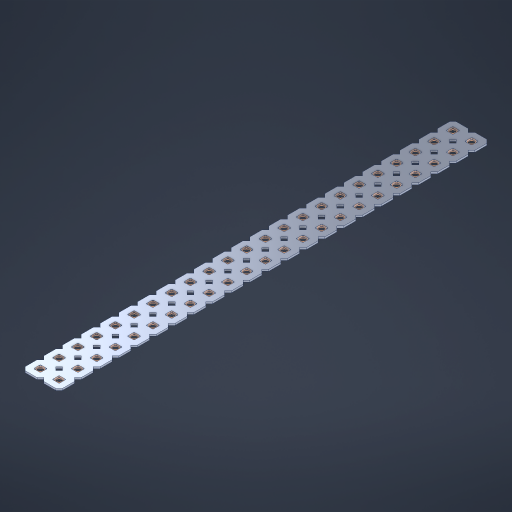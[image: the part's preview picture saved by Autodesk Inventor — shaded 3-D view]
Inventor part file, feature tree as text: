
AUTODESK INVENTOR PART (.ipt)
format: ipt  version: 2023 (Build 270158000, 158)  size: 791,040 bytes
history: native  units: in
note: dims shown in document units (in); Inventor stores cm internally (conversion verified against a paired STEP export)
features: other x47, extrude x45, sketch x2, pattern_linear x1
ambient origin geometry x8: Origin, YZ Plane, XZ Plane, XY Plane, X Axis, Y Axis, Z Axis, Center Point
bodies: Solid1 (feature_tree), Body (feature_tree)
feature tree (95):
  pattern_linear  "Rectangular Pattern1"  Spacing1=0.09in  [1 undecoded]
  sketch  "Sketch1"  dims[d1=0.5in]
  sketch  "Sketch2"  dims[d2=0.182in d3=0.09in d4=0.09in d5=0.09in d6=0.09in d7=0.09in d8=0.09in d9=0.09in d10=0.09in d11=0.02in d13=0.0in d14=0.172in d15=0.0625in d16=0.0in d19=0.5in d22=0.5in]
  other  "Srf1"
  other  "Srf126"
  other  "Srf127"
  other  "Srf128"
  other  "Srf129"
  other  "Srf130"
  other  "Srf131"
  other  "Srf250"
  other  "Srf251"
  other  "Srf252"
  other  "Srf253"
  other  "Srf254"
  other  "Srf255"
  other  "Srf256"
  other  "Srf257"
  other  "Srf258"
  other  "Srf259"
  other  "Srf260"
  other  "Srf261"
  other  "Srf262"
  other  "Srf263"
  other  "Srf264"
  other  "Srf265"
  other  "Srf268"
  other  "Srf269"
  other  "Srf270"
  other  "Srf271"
  other  "Srf272"
  other  "Srf273"
  other  "Srf274"
  other  "Srf275"
  other  "Srf276"
  other  "Srf277"
  other  "Srf278"
  other  "Srf279"
  other  "Srf280"
  other  "Srf281"
  other  "Srf282"
  other  "Srf283"
  other  "Srf284"
  other  "Srf285"
  other  "Srf286"
  other  "Srf287"
  other  "Srf288"
  other  "Srf289"
  other  "Srf290"
  other  "Circle"
  extrude  "ExtrusionSrf126"  Depth=0.09in
  extrude  "ExtrusionSrf127"  Depth=0.09in
  extrude  "ExtrusionSrf128"  Depth=0.09in
  extrude  "ExtrusionSrf129"  Depth=0.09in
  extrude  "ExtrusionSrf130"  Depth=0.09in
  extrude  "ExtrusionSrf131"  Depth=0.09in
  extrude  "ExtrusionSrf250"  Depth=0.09in
  extrude  "ExtrusionSrf251"  Depth=0.02in
  extrude  "ExtrusionSrf252"  TaperAngle=0.0deg  [1 undecoded]
  extrude  "ExtrusionSrf253"  Depth=0.5in
  extrude  "ExtrusionSrf254"  Depth=0.5in TaperAngle=0.0deg
  extrude  "ExtrusionSrf255"  Depth=0.5in
  extrude  "ExtrusionSrf256"  Depth=0.5in
  extrude  "ExtrusionSrf257"  [1 undecoded]
  extrude  "ExtrusionSrf258"  [1 undecoded]
  extrude  "ExtrusionSrf259"  [1 undecoded]
  extrude  "ExtrusionSrf260"  [1 undecoded]
  extrude  "ExtrusionSrf261"  [1 undecoded]
  extrude  "ExtrusionSrf262"  [1 undecoded]
  extrude  "ExtrusionSrf263"  [1 undecoded]
  extrude  "ExtrusionSrf264"  [1 undecoded]
  extrude  "ExtrusionSrf265"  [1 undecoded]
  extrude  "ExtrusionSrf268"  [1 undecoded]
  extrude  "ExtrusionSrf269"  [1 undecoded]
  extrude  "ExtrusionSrf270"  [1 undecoded]
  extrude  "ExtrusionSrf271"  [1 undecoded]
  extrude  "ExtrusionSrf272"  [1 undecoded]
  extrude  "ExtrusionSrf273"  [1 undecoded]
  extrude  "ExtrusionSrf274"  [1 undecoded]
  extrude  "ExtrusionSrf275"  [1 undecoded]
  extrude  "ExtrusionSrf276"  [1 undecoded]
  extrude  "ExtrusionSrf277"  [1 undecoded]
  extrude  "ExtrusionSrf278"  [1 undecoded]
  extrude  "ExtrusionSrf279"  [1 undecoded]
  extrude  "ExtrusionSrf280"  [1 undecoded]
  extrude  "ExtrusionSrf281"  [1 undecoded]
  extrude  "ExtrusionSrf282"  [1 undecoded]
  extrude  "ExtrusionSrf283"  [1 undecoded]
  extrude  "ExtrusionSrf284"  [1 undecoded]
  extrude  "ExtrusionSrf285"  [1 undecoded]
  extrude  "ExtrusionSrf286"  [1 undecoded]
  extrude  "ExtrusionSrf287"  [1 undecoded]
  extrude  "ExtrusionSrf288"  [1 undecoded]
  extrude  "ExtrusionSrf289"  [1 undecoded]
  extrude  "ExtrusionSrf290"  [1 undecoded]
note: 34 required parameter values undecoded (feature->parameter linkage not recoverable at this tier; creation-order binding heuristic only, values carry confidence <= 0.55)
